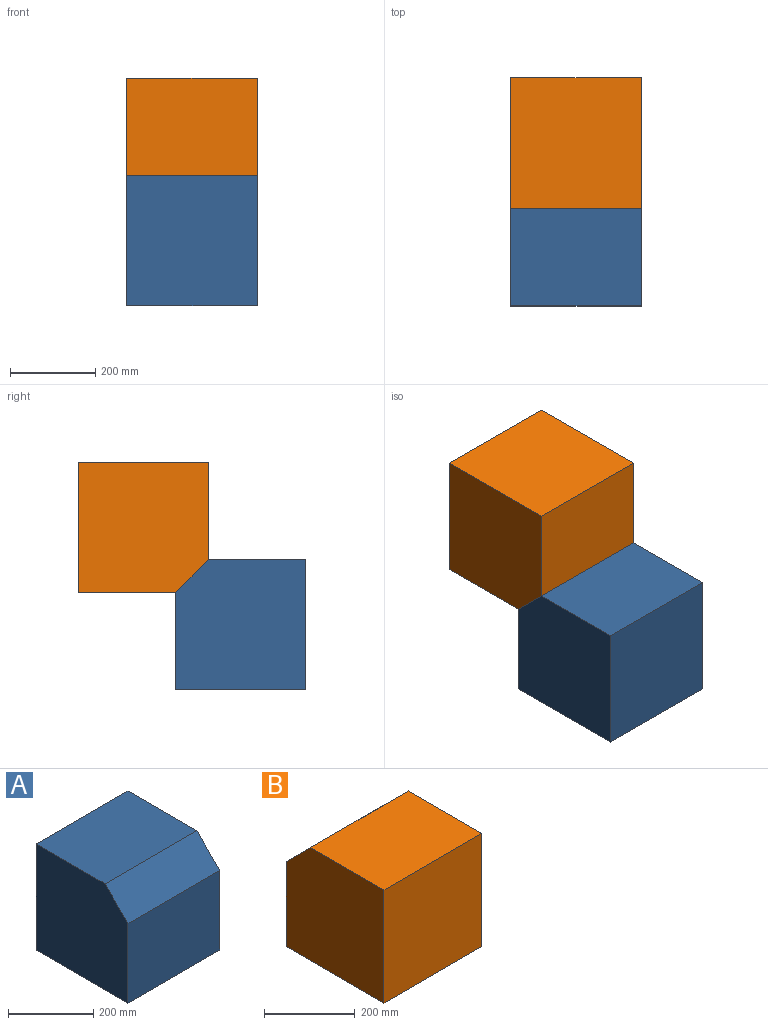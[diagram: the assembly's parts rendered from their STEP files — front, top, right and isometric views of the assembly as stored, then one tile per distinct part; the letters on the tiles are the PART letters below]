
ASSEMBLY  parts=2 mates=1
PART A: 7 faces, bbox 304.8x304.8x304.8 mm
  f0: plane 304.8x304.8mm, normal (-1,0,0), area 89999.8mm2, adj f1,f3,f4,f5,f6
  f1: plane 304.8x304.8mm, normal (0,0,-1), area 92903mm2, adj f0,f2,f4,f5
  f2: plane 304.8x304.8mm, normal (1,0,0), area 89999.8mm2, adj f1,f3,f4,f5,f6
  f3: plane 304.8x228.6mm, normal (0,0,1), area 69677.3mm2, adj f0,f2,f5,f6
  f4: plane 304.8x228.6mm, normal (0,-1,0), area 69677.3mm2, adj f0,f1,f2,f6
  f5: plane 304.8x304.8mm, normal (0,1,0), area 92903mm2, adj f0,f1,f2,f3
  f6: plane 304.8x76.2mm, normal (0,-0.71,0.71), area 32846.2mm2, adj f0,f2,f3,f4
PART B: 7 faces, bbox 304.8x304.8x304.8 mm
  f0: plane 304.8x304.8mm, normal (1,0,0), area 89999.8mm2, adj f1,f3,f4,f5,f6
  f1: plane 304.8x304.8mm, normal (0,0,-1), area 92903mm2, adj f0,f2,f4,f5
  f2: plane 304.8x304.8mm, normal (-1,0,0), area 89999.8mm2, adj f1,f3,f4,f5,f6
  f3: plane 304.8x228.6mm, normal (0,0,1), area 69677.3mm2, adj f0,f2,f5,f6
  f4: plane 304.8x228.6mm, normal (0,1,0), area 69677.3mm2, adj f0,f1,f2,f6
  f5: plane 304.8x304.8mm, normal (0,-1,0), area 92903mm2, adj f0,f1,f2,f3
  f6: plane 304.8x76.2mm, normal (0,0.71,0.71), area 32846.2mm2, adj f0,f2,f3,f4
PLACE A rot(axis=(-1,0,0),90deg) t=(251.68,-555.9,187.38)mm
PLACE B rot(axis=(-1,0,0),180deg) t=(-53.12,-22.5,720.78)mm
MATE fastened A.f6 <-> B.f6  axis (0,0.71,0.71) through (404.08,-289.2,454.08)mm
